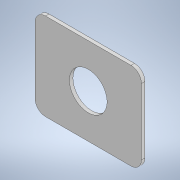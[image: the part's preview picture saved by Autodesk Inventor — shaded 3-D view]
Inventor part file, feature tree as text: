
AUTODESK INVENTOR PART (.ipt)
format: ipt  version: 2020 (Build 240168000, 168)  size: 136,192 bytes
history: native  units: mm
features: other x4, extrude x1, fillet x1, sketch x1
ambient origin geometry x8: Origin, YZ Plane, XZ Plane, XY Plane, X Axis, Y Axis, Z Axis, Center Point
bodies: Solid1 (feature_tree)
feature tree (7):
  other  "screen-dc-port-front.ipt"
  extrude  "Extrusion1"  Depth=1.0mm TaperAngle=0.0deg
  fillet  "Fillet1"  Radius=3.0mm
  other  "TaggingFeature1"
  sketch  "Sketch1"  dims[d0=10.0mm d1=1.0mm d2=0.0mm d3=3.0mm]
  other  "Solid1::screen-dc-port-front.ipt"
  other  "Srf1"
